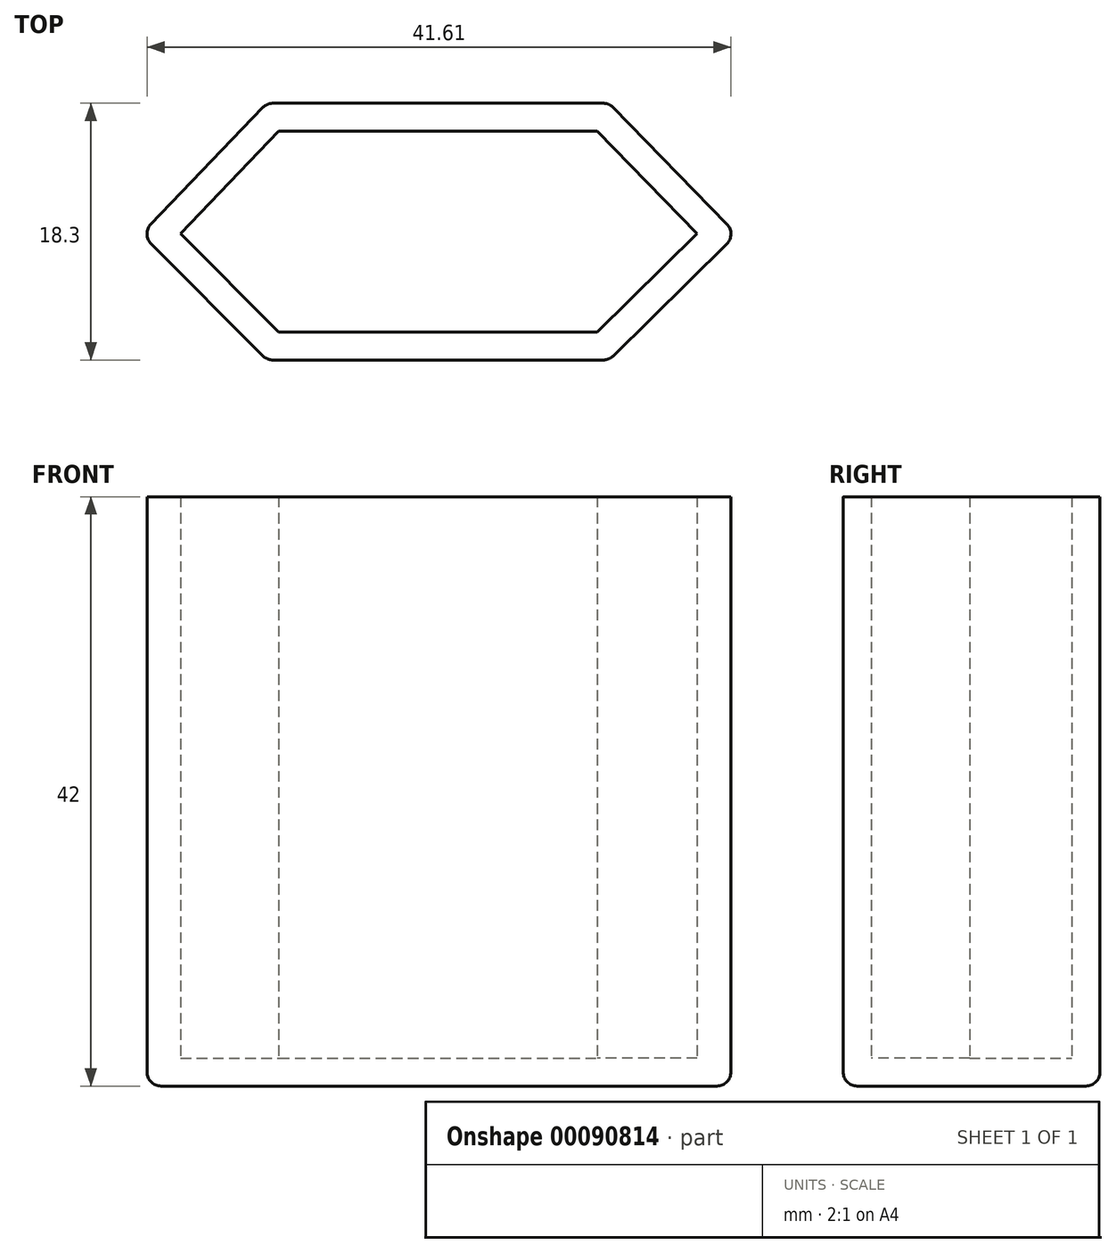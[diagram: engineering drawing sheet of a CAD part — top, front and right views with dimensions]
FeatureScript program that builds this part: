
annotation { "Feature Type Name" : "Feature", "Feature Type Description" : "" }
export const myFeature = defineFeature(function(context is Context, id is Id, definition is map)
    precondition{}
    {
        {
            var Q0;
            Q0=qCreatedBy(makeId("Top.planeOp"),FACE);
            var sketch = newSketch(context, id + "F0", { "sketchPlane" : qUnion([Q0])});
            skLineSegment(sketch, "E0", {"start": v(0, 0) * mm, "end": v(-7.1, 7.3) * mm});
            skLineSegment(sketch, "E1", {"start": v(-7.1, 7.3) * mm, "end": v(-29.8, 7.3) * mm});
            skLineSegment(sketch, "E2", {"start": v(0, 0) * mm, "end": v(-7.1, -7) * mm});
            skLineSegment(sketch, "E3", {"start": v(-29.8, -7) * mm, "end": v(-7.1, -7) * mm});
            skLineSegment(sketch, "E4", {"start": v(-29.8, 7.3) * mm, "end": v(-36.8, 0) * mm});
            skLineSegment(sketch, "E5", {"start": v(-36.8, 0) * mm, "end": v(-29.8, -7) * mm});
            skLineSegment(sketch, "E6.0", {"start": v(2.82, -0.03) * mm, "end": v(-6.26, 9.3) * mm});
            skLineSegment(sketch, "E6.1", {"start": v(-30.66, 9.3) * mm, "end": v(-39.6, -0.03) * mm});
            skLineSegment(sketch, "E6.2", {"start": v(-39.6, -0.03) * mm, "end": v(-30.63, -9) * mm});
            skLineSegment(sketch, "E6.3", {"start": v(-6.26, 9.3) * mm, "end": v(-30.66, 9.3) * mm});
            skLineSegment(sketch, "E6.4", {"start": v(-30.63, -9) * mm, "end": v(-6.28, -9) * mm});
            skLineSegment(sketch, "E6.5", {"start": v(2.82, -0.03) * mm, "end": v(-6.28, -9) * mm});
            skSolve(sketch);
        }
        {
            var Q0;
            Q0 = qSketchRegion(id + "F0", true);
            extrude(context, id + "F1", {"entities" : qUnion([Q0]), "depth" : 42 * mm});
        }
        {
            var Q0;
            Q0=makeQuery(id+"F0.imprint","IMPRINT",FACE,{"disambiguationData":[TD([[makeQuery(id+"F0.imprint","IMPRINT",EDGE,{"derivedFrom":sQuery(id+"F0.wireOp",EDGE,"E0")}),1.0]])]});
            extrude(context, id + "F2", {"entities" : qUnion([Q0]), "operationType" : NewBodyOperationType.ADD, "depth" : 2 * mm});
        }
        {
            var Q0;
            Q0=makeQuery(id+"F1.opExtrude","CAP_EDGE",EDGE,{"disambiguationData":[OSD([sQuery(id+"F0.wireOp",EDGE,"E6.0")])],"isStart":true});
            var Q1;
            Q1=makeQuery(id+"F1.opExtrude","CAP_EDGE",EDGE,{"disambiguationData":[OSD([sQuery(id+"F0.wireOp",EDGE,"E6.3")])],"isStart":true});
            var Q2;
            Q2=makeQuery(id+"F1.opExtrude","CAP_EDGE",EDGE,{"disambiguationData":[OSD([sQuery(id+"F0.wireOp",EDGE,"E6.1")])],"isStart":true});
            var Q3;
            Q3=makeQuery(id+"F1.opExtrude","CAP_EDGE",EDGE,{"disambiguationData":[OSD([sQuery(id+"F0.wireOp",EDGE,"E6.2")])],"isStart":true});
            var Q4;
            Q4=makeQuery(id+"F1.opExtrude","CAP_EDGE",EDGE,{"disambiguationData":[OSD([sQuery(id+"F0.wireOp",EDGE,"E6.4")])],"isStart":true});
            var Q5;
            Q5=makeQuery(id+"F1.opExtrude","CAP_EDGE",EDGE,{"disambiguationData":[OSD([sQuery(id+"F0.wireOp",EDGE,"E6.5")])],"isStart":true});
            fillet(context, id + "F3", {"entities" : qUnion([Q0, Q1, Q2, Q3, Q4, Q5]), "radius" : 1 * mm, "tangentPropagation" : true, "allowEdgeOverflow" : false});
        }
        {
            var Q0;
            Q0=makeQuery(id+"F1.opExtrude","SWEPT_EDGE",EDGE,{"disambiguationData":[OSD([sQuery(id+"F0.wireOp",EDGE,"E6.1"),sQuery(id+"F0.wireOp",EDGE,"E6.2")])]});
            var Q1;
            Q1=makeQuery(id+"F1.opExtrude","SWEPT_EDGE",EDGE,{"disambiguationData":[OSD([sQuery(id+"F0.wireOp",EDGE,"E6.2"),sQuery(id+"F0.wireOp",EDGE,"E6.4")])]});
            var Q2;
            Q2=makeQuery(id+"F1.opExtrude","SWEPT_EDGE",EDGE,{"disambiguationData":[OSD([sQuery(id+"F0.wireOp",EDGE,"E6.4"),sQuery(id+"F0.wireOp",EDGE,"E6.5")])]});
            var Q3;
            Q3=makeQuery(id+"F1.opExtrude","SWEPT_EDGE",EDGE,{"disambiguationData":[OSD([sQuery(id+"F0.wireOp",EDGE,"E6.0"),sQuery(id+"F0.wireOp",EDGE,"E6.5")])]});
            var Q4;
            Q4=makeQuery(id+"F1.opExtrude","SWEPT_EDGE",EDGE,{"disambiguationData":[OSD([sQuery(id+"F0.wireOp",EDGE,"E6.0"),sQuery(id+"F0.wireOp",EDGE,"E6.3")])]});
            var Q5;
            Q5=makeQuery(id+"F1.opExtrude","SWEPT_EDGE",EDGE,{"disambiguationData":[OSD([sQuery(id+"F0.wireOp",EDGE,"E6.1"),sQuery(id+"F0.wireOp",EDGE,"E6.3")])]});
            fillet(context, id + "F4", {"entities" : qUnion([Q0, Q1, Q2, Q3, Q4, Q5]), "radius" : 1 * mm, "tangentPropagation" : true, "allowEdgeOverflow" : false});
        }
    });
